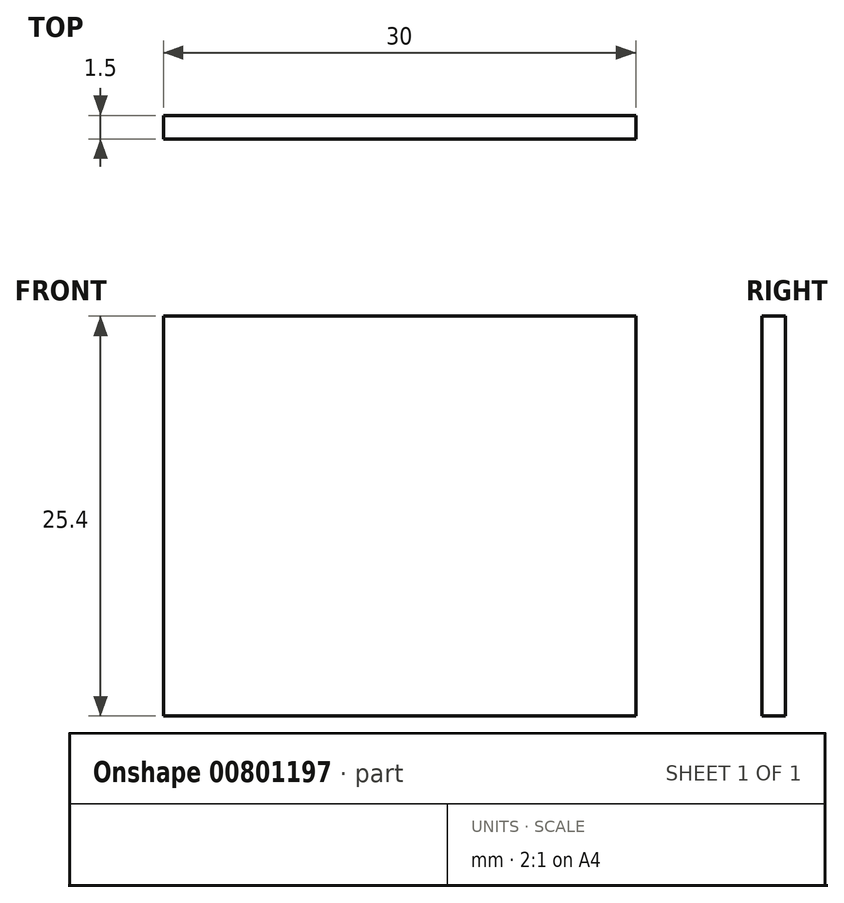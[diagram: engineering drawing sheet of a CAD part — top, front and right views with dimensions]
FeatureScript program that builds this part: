
annotation { "Feature Type Name" : "Feature", "Feature Type Description" : "" }
export const myFeature = defineFeature(function(context is Context, id is Id, definition is map)
    precondition{}
    {
        {
            var Q0;
            Q0=qCreatedBy(makeId("Top.planeOp"),FACE);
            var sketch = newSketch(context, id + "F0", { "sketchPlane" : qUnion([Q0])});
            skLineSegment(sketch, "E0.bottom", {"start": v(-10.15, -7.77) * mm, "end": v(19.85, -7.77) * mm});
            skLineSegment(sketch, "E0.top", {"start": v(-10.15, -9.27) * mm, "end": v(19.85, -9.27) * mm});
            skLineSegment(sketch, "E0.left", {"start": v(-10.15, -7.77) * mm, "end": v(-10.15, -9.27) * mm});
            skLineSegment(sketch, "E0.right", {"start": v(19.85, -7.77) * mm, "end": v(19.85, -9.27) * mm});
            skSolve(sketch);
        }
        {
            var Q0;
            Q0 = qSketchRegion(id + "F0", true);
            extrude(context, id + "F1", {"entities" : qUnion([Q0]), "depth" : 25.4 * mm, "offsetDistance" : 25.4 * mm});
        }
    });
